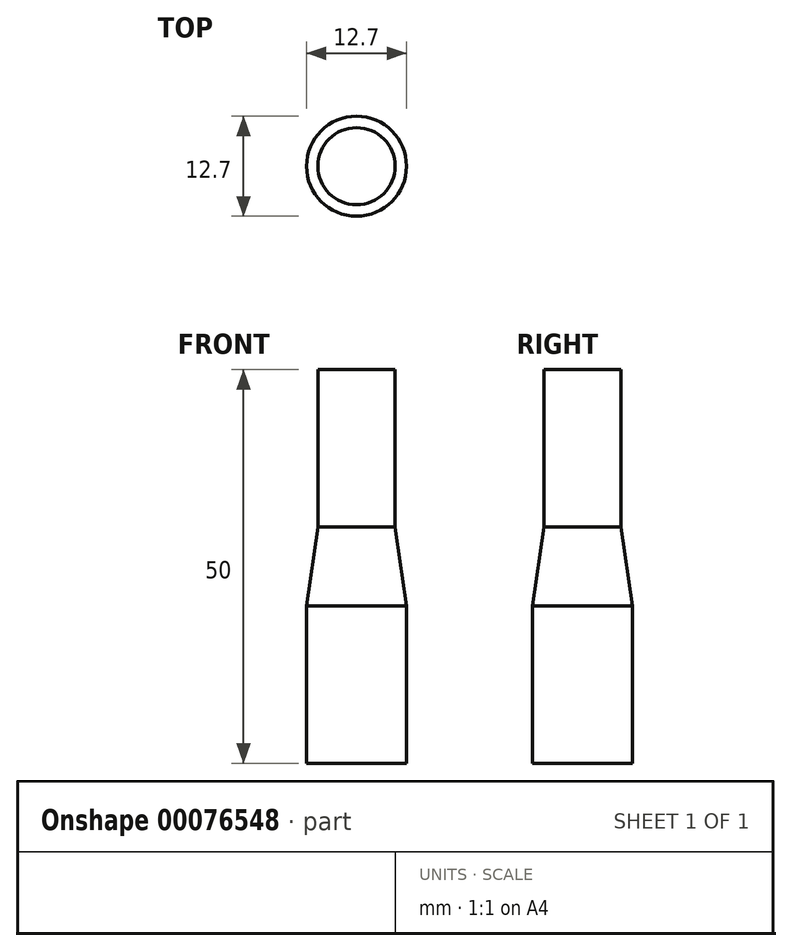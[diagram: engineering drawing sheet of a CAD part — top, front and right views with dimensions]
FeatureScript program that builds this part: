
annotation { "Feature Type Name" : "Feature", "Feature Type Description" : "" }
export const myFeature = defineFeature(function(context is Context, id is Id, definition is map)
    precondition{}
    {
        {
            var Q0;
            Q0=qCreatedBy(makeId("Right.planeOp"),FACE);
            var sketch = newSketch(context, id + "F0", { "sketchPlane" : qUnion([Q0])});
            skLineSegment(sketch, "E0.bottom", {"start": v(0, 25) * mm, "end": v(-4.9, 25) * mm});
            skLineSegment(sketch, "E0.top", {"start": v(0, -25) * mm, "end": v(-6.17, -25) * mm});
            skLineSegment(sketch, "E0.left", {"start": v(0, 25) * mm, "end": v(0, -25) * mm});
            skLineSegment(sketch, "E0.right", {"start": v(-4.9, 25) * mm, "end": v(-4.9, 5) * mm});
            skLineSegment(sketch, "E1.top", {"start": v(0, -25) * mm, "end": v(-6.35, -25) * mm});
            skLineSegment(sketch, "E1.left", {"start": v(0, -5.1) * mm, "end": v(0, -25) * mm});
            skLineSegment(sketch, "E1.right", {"start": v(-6.35, -5) * mm, "end": v(-6.35, -25) * mm});
            skLineSegment(sketch, "E2", {"start": v(-6.35, -5) * mm, "end": v(-4.9, 5) * mm});
            skLineSegment(sketch, "E3", {"start": v(0, 0) * mm, "end": v(-23.06, 0) * mm, "construction": true});
            skLineSegment(sketch, "E4", {"start": v(-22.67, 5) * mm, "end": v(0, 5) * mm, "construction": true});
            skLineSegment(sketch, "E5", {"start": v(-22.81, -5) * mm, "end": v(0, -5) * mm, "construction": true});
            skLineSegment(sketch, "E6", {"start": v(0, 38.1) * mm, "end": v(0, -49.67) * mm, "construction": true});
            skSolve(sketch);
        }
        {
            var Q0;
            Q0=makeQuery(id+"F0.imprint","IMPRINT",FACE,{"disambiguationData":[TD([[makeQuery(id+"F0.imprint","IMPRINT",EDGE,{"derivedFrom":sQuery(id+"F0.wireOp",EDGE,"E0.bottom")}),1.0]])]});
            var Q1;
            Q1=sQuery(id+"F0.wireOp",EDGE,"E6");
            revolve(context, id + "F1", {"entities" : qUnion([Q0]), "axis" : qUnion([Q1]), "revolveType" : RevolveType.FULL});
        }
    });
